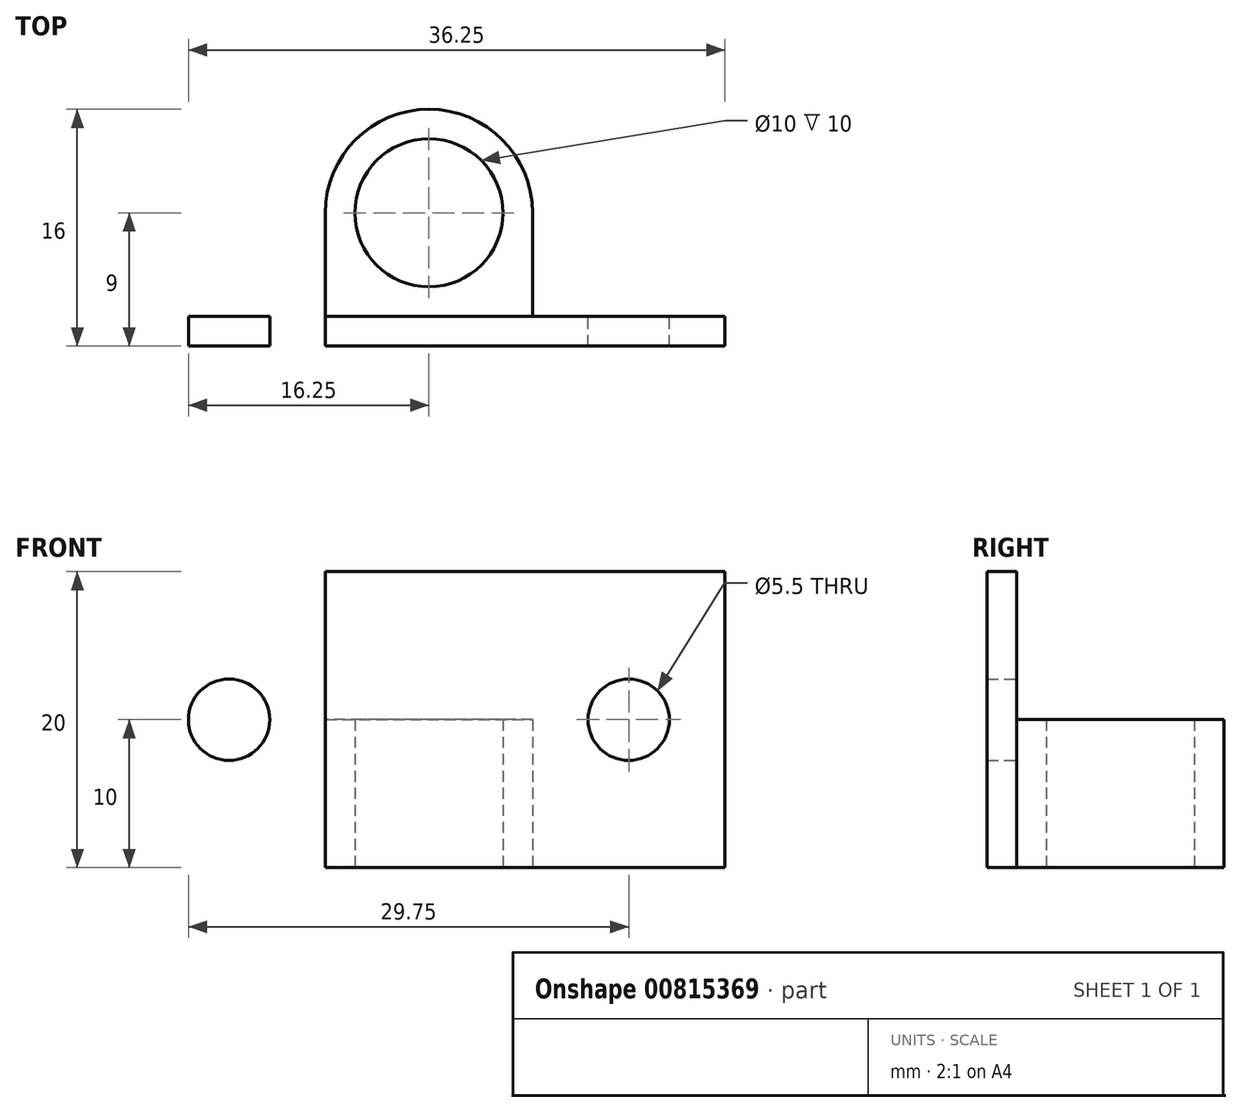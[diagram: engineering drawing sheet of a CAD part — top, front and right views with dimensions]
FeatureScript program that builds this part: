
annotation { "Feature Type Name" : "Feature", "Feature Type Description" : "" }
export const myFeature = defineFeature(function(context is Context, id is Id, definition is map)
    precondition{}
    {
        {
            var Q0;
            Q0=qCreatedBy(makeId("Top.planeOp"),FACE);
            var sketch = newSketch(context, id + "F0", { "sketchPlane" : qUnion([Q0])});
            skLineSegment(sketch, "E0", {"start": v(0, 0) * mm, "end": v(0, -2) * mm, "construction": true});
            skPoint(sketch, "E1", {"position": v(0, -1) * mm});
            skLineSegment(sketch, "E2.bottom", {"start": v(20, -2) * mm, "end": v(-20, -2) * mm});
            skLineSegment(sketch, "E2.top", {"start": v(20, 0) * mm, "end": v(-20, 0) * mm});
            skLineSegment(sketch, "E2.left", {"start": v(20, -2) * mm, "end": v(20, 0) * mm});
            skLineSegment(sketch, "E2.right", {"start": v(-20, -2) * mm, "end": v(-20, 0) * mm});
            skCircle(sketch, "E3", {"center": v(0, 7) * mm, "radius": 5 * mm});
            skCircle(sketch, "E4.0", {"center": v(0, 7) * mm, "radius": 7 * mm});
            skLineSegment(sketch, "E5", {"start": v(-7, 7) * mm, "end": v(-7, 0) * mm});
            skLineSegment(sketch, "E6", {"start": v(7, 7) * mm, "end": v(7, 0) * mm});
            skSolve(sketch);
        }
        {
            var Q0;
            Q0 = qSketchRegion(id + "F0", true);
            extrude(context, id + "F1", {"entities" : qUnion([Q0]), "depth" : 20 * mm, "offsetDistance" : 25 * mm});
        }
        {
            var Q0;
            {var subQ0=sQuery(id+"F0.wireOp",EDGE,"E2.top");Q0=makeQuery(id+"F1.opExtrude","SWEPT_FACE",FACE,{"disambiguationData":[OSD([subQ0]),TDD([makeQuery(id+"F0.imprint","IMPRINT",EDGE,{"disambiguationData":[TD([[makeQuery(id+"F0.imprint","INTERSECT",VERTEX,{"derivedFrom":[subQ0,sQuery(id+"F0.wireOp",EDGE,"E2.right")]}),1.0]])],"derivedFrom":subQ0})])]});}
            var sketch = newSketch(context, id + "F2", { "sketchPlane" : qUnion([Q0])});
            skLineSegment(sketch, "E7.0", {"start": v(-7, 20) * mm, "end": v(-7, 0) * mm, "construction": true});
            skLineSegment(sketch, "E8.0", {"start": v(-20, 20) * mm, "end": v(-20, 0) * mm, "construction": true});
            skLineSegment(sketch, "E9", {"start": v(-20, 20) * mm, "end": v(-7, 0) * mm, "construction": true});
            skCircle(sketch, "E10", {"center": v(-13.5, 10) * mm, "radius": 2.75 * mm});
            skCircle(sketch, "E11.MirrorC", {"center": v(13.5, 10) * mm, "radius": 2.75 * mm});
            skSolve(sketch);
        }
        {
            var Q0;
            Q0=makeQuery(id+"F2.imprint","IMPRINT",FACE,{"disambiguationData":[TD([[makeQuery(id+"F2.imprint","IMPRINT",EDGE,{"derivedFrom":sQuery(id+"F2.wireOp",EDGE,"E10")}),1.0]])]});
            var Q1;
            Q1=makeQuery(id+"F2.imprint","IMPRINT",FACE,{"disambiguationData":[TD([[makeQuery(id+"F2.imprint","IMPRINT",EDGE,{"derivedFrom":sQuery(id+"F2.wireOp",EDGE,"E11.MirrorC")}),-1.0]])]});
            extrude(context, id + "F3", {"entities" : qUnion([Q0, Q1]), "operationType" : NewBodyOperationType.REMOVE, "endBound" : BoundingType.UP_TO_NEXT, "oppositeDirection" : true, "depth" : 25 * mm, "offsetDistance" : 25 * mm});
        }
        {
            var Q0;
            Q0=makeQuery(id+"F1.opExtrude","CAP_FACE",FACE,{"disambiguationData":[OSD([sQuery(id+"F0.wireOp",EDGE,"L2DenR6S-WREx-wRR0-acmL-UfIBoBumMS3j"),sQuery(id+"F0.wireOp",EDGE,"8b35ebcf-eff3-4e24-b810-ddf77919ef88.0"),sQuery(id+"F0.wireOp",EDGE,"E2.bottom"),sQuery(id+"F0.wireOp",EDGE,"E2.top"),sQuery(id+"F0.wireOp",EDGE,"E2.left"),sQuery(id+"F0.wireOp",EDGE,"E2.right")])],"isStart":false});
            var sketch = newSketch(context, id + "F4", { "sketchPlane" : qUnion([Q0])});
            skLineSegment(sketch, "E12.0", {"start": v(20, 0) * mm, "end": v(7, 0) * mm});
            skLineSegment(sketch, "E13.0", {"start": v(-7, 0) * mm, "end": v(-20, 0) * mm});
            skLineSegment(sketch, "E14.bottom", {"start": v(-7, 0) * mm, "end": v(7, 0) * mm});
            skLineSegment(sketch, "E14.top", {"start": v(-7, 14) * mm, "end": v(7, 14) * mm});
            skLineSegment(sketch, "E14.left", {"start": v(-7, 0) * mm, "end": v(-7, 14) * mm});
            skLineSegment(sketch, "E14.right", {"start": v(7, 0) * mm, "end": v(7, 14) * mm});
            skArc(sketch, "E15.0", {"start": v(7, 7) * mm, "mid": v(0, 14) * mm, "end": v(-7, 7) * mm});
            skSolve(sketch);
        }
        {
            var Q0;
            Q0 = qSketchRegion(id + "F4", true);
            extrude(context, id + "F5", {"entities" : qUnion([Q0]), "operationType" : NewBodyOperationType.REMOVE, "oppositeDirection" : true, "depth" : 10 * mm, "offsetDistance" : 25 * mm});
        }
    });
